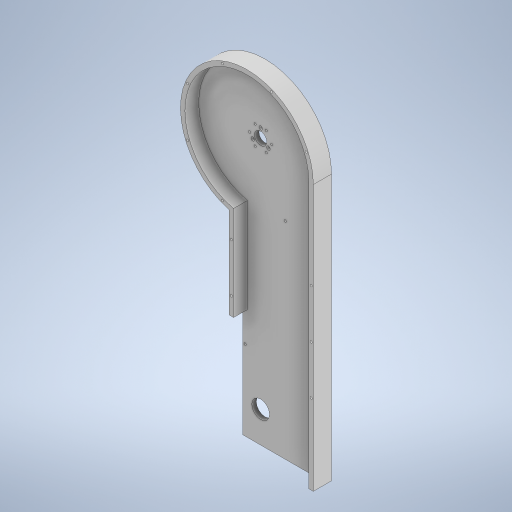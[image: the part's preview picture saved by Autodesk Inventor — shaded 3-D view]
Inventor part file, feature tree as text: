
AUTODESK INVENTOR PART (.ipt)
format: ipt  version: 2024.3 (Build 283343000, 343)  size: 430,592 bytes
history: native  units: mm
features: sketch x11, extrude x6, hole x5, other x1
ambient origin geometry x8: Origin, YZ Plane, XZ Plane, XY Plane, X Axis, Y Axis, Z Axis, Center Point
bodies: Body1 (feature_tree)
feature tree (23):
  other  "ソリッド1"
  extrude  "押し出し1"  Depth=150.0mm
  hole  "穴1"  [1 undecoded]
  extrude  "押し出し2"  Depth=20.5mm TaperAngle=0.0deg
  extrude  "押し出し3"  Depth=145.0mm
  extrude  "押し出し4"  TaperAngle=22.5deg  [1 undecoded]
  hole  "穴2"  [1 undecoded]
  hole  "穴3"  [1 undecoded]
  hole  "穴4"  [1 undecoded]
  hole  "穴5"  [1 undecoded]
  extrude  "押し出し12"  Depth=150.0mm
  extrude  "押し出し13"  Depth=300.0mm
  sketch  "スケッチ1"
  sketch  "スケッチ2"
  sketch  "スケッチ3"
  sketch  "スケッチ4"
  sketch  "スケッチ5"
  sketch  "スケッチ6"
  sketch  "スケッチ7"
  sketch  "スケッチ13"
  sketch  "スケッチ14"
  sketch  "スケッチ17"
  sketch  "スケッチ19"
note: 6 required parameter values undecoded (feature->parameter linkage not recoverable at this tier; creation-order binding heuristic only, values carry confidence <= 0.55)
